# Revit family: RA 11 DIXIT LED OSCILLANTE
name_source: partatom
category: Lighting Fixtures
units: mm (PartAtom-declared; Revit-internal decimal feet)

## family parameters
Always vertical = Yes
Cut with Voids When Loaded = No
Host = Ceiling
Light Source = No
OmniClass Number = 23.80.70.11
OmniClass Title = Luminaries for Internal Lighting
Part Type = Normal
Room Calculation Point = No
Round Connector Dimension = Use Diameter
Shared = No

## types (1)
- RA 11 DIXIT LED OSCILLANTE
    Beam angle (°) = 0
    Body angle = 20.00°
    Body material = White Powder Coated Aluminium
    Description = La gamma di incassi oscillanti RA 11 Dixit LED è stata progettata per soddisfare le più diverse esigenze illuminotecniche, in particolare per l'applicazione in centri commerciali, negozi e uffici.
L'elevato rendimento luminoso di RA 11 Dixit LED si coniuga con contenuti valori di luminanza e livelli di abbagliamento estremamente bassi, consentendo un ottimo comfort visivo.
Driver da ordinare separatamente; la potenzza dell'apparecchio varia a seconda del driver scelto.
    Glass material = Glass
    Larghezza = 125 mm
    Manufacturer = ARIA
    Model = 256-200
    Type = RA 11 body : RA 11 DIXIT LED OSCILLANTE 2450lm 18W 4000K CRI85-70° WHITE
    Type Comments = Ceiling recessed light
    Type Image = RA11DIXIT_LED_ADJ_TAB-Sito-Ivela.jpg
    URL = https://www.aria.lighting

## geometry (parser evidence)
native form markers: Sweep x5
no freeform markers — native parametric forms only
